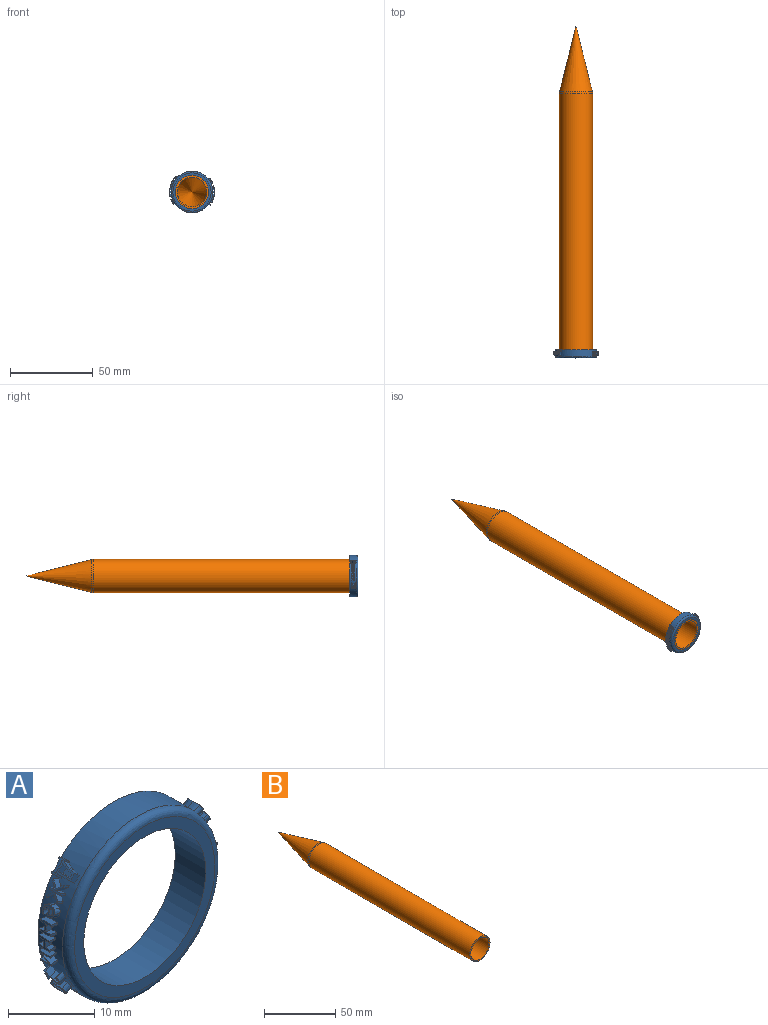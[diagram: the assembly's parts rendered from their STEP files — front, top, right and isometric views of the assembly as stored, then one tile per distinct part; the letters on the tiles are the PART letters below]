
ASSEMBLY  parts=2 mates=1
PART A: 316 faces, bbox 27x5x25 mm
  f0: plane 2.34x0.83mm, normal (0.55,0,0.83), area 2.3mm2, adj f1,f9,f10,f32
  f1: plane 0.98x0.78mm, normal (0,-1,0), area 0.3mm2, adj f0,f2,f10,f32
  f2: plane 2.36x0.83mm, normal (-0.55,0,-0.83), area 2.4mm2, adj f1,f3,f10,f32
  f3: extruded ~0.88x0.62mm, area 0.3mm2, adj f2,f4,f10,f32
  f4: extruded ~0.97x0.76mm, area 0.3mm2, adj f3,f5,f10,f32
  f5: extruded ~0.97x0.76mm, area 0.2mm2, adj f4,f6,f10,f32
  f6: plane 0.84x0.55mm, normal (-0.55,0,-0.83), area 0.2mm2, adj f5,f7,f10,f32
  f7: extruded ~0.97x0.76mm, area 0.2mm2, adj f6,f8,f10,f32
  f8: extruded ~1.09x0.93mm, area 0.5mm2, adj f7,f9,f10,f32
  f9: extruded ~0.92x0.68mm, area 0.5mm2, adj f0,f8,f10,f32
  f10: cylinder r=13.5mm len=2.98mm, axis (0,1,0), area 0.9mm2, adj f0,f1,f2,f3,f4,f5,f6,f7
  f11: extruded ~1.03x0.69mm, area 0.3mm2, adj f12,f24,f30,f32
  f12: extruded ~1.04x0.72mm, area 0.3mm2, adj f11,f13,f30,f32
  f13: extruded ~1.18x1mm, area 0.7mm2, adj f12,f14,f30,f32
  f14: extruded ~1.01x0.66mm, area 0.7mm2, adj f13,f15,f30,f32
  f15: extruded ~1x0.68mm, area 0.7mm2, adj f14,f16,f30,f32
  f16: extruded ~1.16x0.95mm, area 0.6mm2, adj f15,f17,f30,f32
  f17: extruded ~1.14x0.92mm, area 0.6mm2, adj f16,f18,f30,f32
  f18: extruded ~0.99x0.62mm, area 0.6mm2, adj f17,f19,f30,f32
  f19: plane 0.9x0.44mm, normal (0.44,0,0.9), area 0.2mm2, adj f18,f20,f30,f32
  f20: plane 1.54x1.43mm, normal (0,1,0), area 1.2mm2, adj f19,f21,f30,f32
  f21: extruded ~0.97x0.58mm, area 0.5mm2, adj f20,f22,f30,f32
  f22: extruded ~1.09x0.82mm, area 0.5mm2, adj f21,f23,f30,f32
  f23: extruded ~1.16x0.96mm, area 0.6mm2, adj f22,f24,f30,f32
  f24: plane 0.9x0.44mm, normal (0.44,0,0.9), area 0.2mm2, adj f11,f23,f30,f32
  f25: plane 1.31x1.27mm, normal (0,-1,0), area 0.9mm2, adj f26,f29,f30,f31
  f26: extruded ~0.97x0.58mm, area 0.4mm2, adj f25,f27,f30,f31
  f27: extruded ~1.05x0.75mm, area 0.4mm2, adj f26,f28,f30,f31
  f28: extruded ~1.04x0.73mm, area 0.4mm2, adj f27,f29,f30,f31
  f29: extruded ~0.95x0.54mm, area 0.4mm2, adj f25,f28,f30,f31
  f30: cylinder r=13.5mm len=1.83mm, axis (0,1,0), area 1.2mm2, adj f11,f12,f13,f14,f15,f16,f17,f18
  f31: cylinder r=12.5mm len=0.83mm, axis (0,1,0), area 0.4mm2, adj f25,f26,f27,f28,f29
  f32: cylinder r=12.5mm len=25mm, axis (0,1,0), area 286.3mm2, adj f0,f1,f2,f3,f4,f5,f6,f7
  f33: plane 1.21x0.95mm, normal (0.3,0,0.95), area 1.2mm2, adj f32,f34,f51,f60
  f34: plane 1.01x0.5mm, normal (0,1,0), area 0.2mm2, adj f32,f33,f35,f60
  f35: plane 0.97x0.36mm, normal (-0.3,0.21,-0.93), area 0.3mm2, adj f32,f34,f36,f60
  f36: plane 0.96x0.32mm, normal (0,1,0), area 0mm2, adj f32,f35,f37,f60
  f37: extruded ~1.04x0.56mm, area 0.4mm2, adj f32,f36,f38,f60
  f38: extruded ~1.05x0.62mm, area 0.3mm2, adj f32,f37,f39,f60
  f39: extruded ~1.09x0.7mm, area 0.4mm2, adj f32,f38,f40,f60
  f40: extruded ~1.01x0.45mm, area 0.4mm2, adj f32,f39,f41,f60
  f41: extruded ~1.23x1.13mm, area 1.2mm2, adj f32,f40,f42,f60
  f42: plane 1.04x0.59mm, normal (-0.01,-1,-0.03), area 0.3mm2, adj f32,f41,f43,f60
  f43: plane 0.95x0.31mm, normal (-0.3,0,-0.95), area 0.1mm2, adj f32,f42,f44,f60
  f44: extruded ~0.98x0.39mm, area 0.3mm2, adj f32,f43,f45,f60
  f45: extruded ~1.04x0.58mm, area 0.3mm2, adj f32,f44,f46,f60
  f46: extruded ~1.11x0.78mm, area 0.5mm2, adj f32,f45,f47,f60
  f47: plane 0.98x0.38mm, normal (-0.28,0.37,-0.88), area 0.2mm2, adj f32,f46,f48,f60
  f48: extruded ~1.05x0.58mm, area 0.3mm2, adj f32,f47,f49,f60
  f49: extruded ~1.05x0.6mm, area 0.3mm2, adj f32,f48,f50,f60
  f50: extruded ~1.11x0.75mm, area 0.5mm2, adj f32,f49,f51,f60
  f51: extruded ~1.01x0.45mm, area 0.5mm2, adj f32,f33,f50,f60
  f52: extruded ~1x0.44mm, area 0.3mm2, adj f53,f59,f60,f61
  f53: extruded ~1.1x0.74mm, area 0.5mm2, adj f52,f54,f60,f61
  f54: plane 1.03x0.56mm, normal (0.01,1,0.04), area 0.3mm2, adj f53,f55,f60,f61
  f55: plane 0.95x0.31mm, normal (-0.3,0,-0.95), area 0.2mm2, adj f54,f56,f60,f61
  f56: extruded ~1x0.44mm, area 0.4mm2, adj f55,f57,f60,f61
  f57: extruded ~1.07x0.68mm, area 0.4mm2, adj f56,f58,f60,f61
  f58: extruded ~1.03x0.54mm, area 0.3mm2, adj f57,f59,f60,f61
  f59: extruded ~0.98x0.39mm, area 0.2mm2, adj f52,f58,f60,f61
  f60: cylinder r=13.5mm len=1.83mm, axis (0,1,0), area 1.2mm2, adj f33,f34,f35,f36,f37,f38,f39,f40
  f61: cylinder r=12.5mm len=0.83mm, axis (0,1,0), area 0.4mm2, adj f52,f53,f54,f55,f56,f57,f58,f59
  f62: extruded ~1.02x0.49mm, area 0.5mm2, adj f32,f63,f78,f79
  f63: extruded ~1.08x0.64mm, area 0.5mm2, adj f32,f62,f64,f79
  f64: extruded ~1.04x0.49mm, area 0.3mm2, adj f32,f63,f65,f79
  f65: extruded ~1.03x0.39mm, area 0.3mm2, adj f32,f64,f66,f79
  f66: plane 0.99x0.17mm, normal (0,-1,0), area 0mm2, adj f32,f65,f67,f79
  f67: plane 1x0.24mm, normal (0.16,-0.18,0.97), area 0.2mm2, adj f32,f66,f68,f79
  f68: plane 1.03x0.37mm, normal (0,-1,0), area 0.2mm2, adj f32,f67,f69,f79
  f69: plane 1.77x0.99mm, normal (-0.16,0,-0.99), area 1.8mm2, adj f32,f68,f70,f79
  f70: plane 1.04x0.42mm, normal (0,1,0), area 0.3mm2, adj f32,f69,f71,f79
  f71: plane 0.99x0.93mm, normal (0.16,0,0.99), area 0.9mm2, adj f32,f70,f72,f79
  f72: extruded ~1.01x0.5mm, area 0.5mm2, adj f32,f71,f73,f79
  f73: extruded ~1.06x0.56mm, area 0.4mm2, adj f32,f72,f74,f79
  f74: extruded ~1.04x0.46mm, area 0.3mm2, adj f32,f73,f75,f79
  f75: extruded ~1.01x0.32mm, area 0.3mm2, adj f32,f74,f76,f79
  f76: plane 1.14x0.99mm, normal (-0.16,0,-0.99), area 1.1mm2, adj f32,f75,f77,f79
  f77: plane 1.02x0.43mm, normal (0,1,0), area 0.3mm2, adj f32,f76,f78,f79
  f78: plane 1.15x0.99mm, normal (0.16,0,0.99), area 1.2mm2, adj f32,f62,f77,f79
  f79: cylinder r=13.5mm len=1.8mm, axis (0,1,0), area 1.1mm2, adj f62,f63,f64,f65,f66,f67,f68,f69
  f80: extruded ~1.01x0.49mm, area 0.5mm2, adj f32,f81,f96,f97
  f81: extruded ~1.02x0.48mm, area 0.5mm2, adj f32,f80,f82,f97
  f82: extruded ~1x0.33mm, area 0.3mm2, adj f32,f81,f83,f97
  f83: extruded ~1.01x0.23mm, area 0.3mm2, adj f32,f82,f84,f97
  f84: plane 1x0.01mm, normal (0,-1,0), area 0mm2, adj f32,f83,f85,f97
  f85: plane 1x0.24mm, normal (0,-0.18,0.98), area 0.2mm2, adj f32,f84,f86,f97
  f86: plane 1.01x0.22mm, normal (0,-1,0), area 0.2mm2, adj f32,f85,f87,f97
  f87: plane 1.77x1mm, normal (0,0,-1), area 1.8mm2, adj f32,f86,f88,f97
  f88: plane 1.01x0.27mm, normal (0,1,0), area 0.3mm2, adj f32,f87,f89,f97
  f89: plane 1x0.93mm, normal (0,0,1), area 0.9mm2, adj f32,f88,f90,f97
  f90: extruded ~1x0.5mm, area 0.5mm2, adj f32,f89,f91,f97
  f91: extruded ~1x0.41mm, area 0.4mm2, adj f32,f90,f92,f97
  f92: extruded ~1.01x0.31mm, area 0.3mm2, adj f32,f91,f93,f97
  f93: extruded ~1x0.32mm, area 0.3mm2, adj f32,f92,f94,f97
  f94: plane 1.14x1mm, normal (0,0,-1), area 1.1mm2, adj f32,f93,f95,f97
  f95: plane 1.01x0.27mm, normal (0,1,0), area 0.3mm2, adj f32,f94,f96,f97
  f96: plane 1.15x1mm, normal (0,0,1), area 1.2mm2, adj f32,f80,f95,f97
  f97: cylinder r=13.5mm len=1.8mm, axis (0,1,0), area 1.1mm2, adj f80,f81,f82,f83,f84,f85,f86,f87
  f98: plane 1.77x0.99mm, normal (0.11,0,-0.99), area 1.8mm2, adj f32,f99,f101,f102
  f99: plane 1.02x0.38mm, normal (0,1,0), area 0.3mm2, adj f32,f98,f100,f102
  f100: plane 1.77x0.99mm, normal (-0.11,0,0.99), area 1.8mm2, adj f32,f99,f101,f102
  f101: plane 1.02x0.38mm, normal (0,-1,0), area 0.3mm2, adj f32,f98,f100,f102
  f102: cylinder r=13.5mm len=1.77mm, axis (0,1,0), area 0.5mm2, adj f98,f99,f100,f101
  f103: extruded ~1.01x0.22mm, area 0.1mm2, adj f32,f104,f110,f111
  f104: extruded ~1x0.16mm, area 0.1mm2, adj f32,f103,f105,f111
  f105: extruded ~1x0.16mm, area 0.1mm2, adj f32,f104,f106,f111
  f106: extruded ~1.01x0.22mm, area 0.1mm2, adj f32,f105,f107,f111
  f107: extruded ~1.01x0.22mm, area 0.1mm2, adj f32,f106,f108,f111
  f108: extruded ~1x0.15mm, area 0.1mm2, adj f32,f107,f109,f111
  f109: extruded ~1x0.15mm, area 0.1mm2, adj f32,f108,f110,f111
  f110: extruded ~1.01x0.22mm, area 0.1mm2, adj f32,f103,f109,f111
  f111: cylinder r=13.5mm len=0.36mm, axis (0,1,0), area 0.1mm2, adj f103,f104,f105,f106,f107,f108,f109,f110
  f112: extruded ~1.05x0.48mm, area 0.3mm2, adj f32,f113,f125,f131
  f113: extruded ~1.05x0.52mm, area 0.3mm2, adj f32,f112,f114,f131
  f114: extruded ~1.12x0.82mm, area 0.7mm2, adj f32,f113,f115,f131
  f115: extruded ~1.04x0.66mm, area 0.7mm2, adj f32,f114,f116,f131
  f116: extruded ~1.03x0.68mm, area 0.7mm2, adj f32,f115,f117,f131
  f117: extruded ~1.11x0.77mm, area 0.6mm2, adj f32,f116,f118,f131
  f118: extruded ~1.1x0.73mm, area 0.6mm2, adj f32,f117,f119,f131
  f119: extruded ~1.03x0.58mm, area 0.6mm2, adj f32,f118,f120,f131
  f120: plane 0.98x0.22mm, normal (-0.22,0,0.98), area 0.2mm2, adj f32,f119,f121,f131
  f121: plane 1.4x1.25mm, normal (0,1,0), area 1.2mm2, adj f32,f120,f122,f131
  f122: extruded ~1.02x0.47mm, area 0.5mm2, adj f32,f121,f123,f131
  f123: extruded ~1.07x0.63mm, area 0.5mm2, adj f32,f122,f124,f131
  f124: extruded ~1.11x0.77mm, area 0.6mm2, adj f32,f123,f125,f131
  f125: plane 0.98x0.24mm, normal (-0.22,0,0.98), area 0.2mm2, adj f32,f112,f124,f131
  f126: plane 1.18x1.12mm, normal (0,-1,0), area 0.9mm2, adj f127,f130,f131,f132
  f127: extruded ~1.01x0.38mm, area 0.4mm2, adj f126,f128,f131,f132
  f128: extruded ~1.05x0.55mm, area 0.4mm2, adj f127,f129,f131,f132
  f129: extruded ~1.05x0.53mm, area 0.4mm2, adj f128,f130,f131,f132
  f130: extruded ~1x0.39mm, area 0.4mm2, adj f126,f129,f131,f132
  f131: cylinder r=13.5mm len=1.83mm, axis (0,1,0), area 1.2mm2, adj f112,f113,f114,f115,f116,f117,f118,f119
  f132: cylinder r=12.5mm len=0.9mm, axis (0,1,0), area 0.4mm2, adj f126,f127,f128,f129,f130
  f133: plane 0.9x0.45mm, normal (-0.45,0,0.9), area 0mm2, adj f32,f134,f152,f153
  f134: plane 1.12x0.91mm, normal (-0.31,0.71,0.63), area 0.7mm2, adj f32,f133,f135,f153
  f135: extruded ~1.12x0.87mm, area 0.7mm2, adj f32,f134,f136,f153
  f136: extruded ~0.96x0.56mm, area 0.5mm2, adj f32,f135,f137,f153
  f137: extruded ~0.99x0.62mm, area 0.5mm2, adj f32,f136,f138,f153
  f138: extruded ~1.14x0.92mm, area 0.6mm2, adj f32,f137,f139,f153
  f139: extruded ~1.23x1.09mm, area 0.8mm2, adj f32,f138,f140,f153
  f140: plane 0.95x0.58mm, normal (0.35,0.61,-0.71), area 0.2mm2, adj f32,f139,f141,f153
  f141: extruded ~1.04x0.71mm, area 0.3mm2, adj f32,f140,f142,f153
  f142: extruded ~1.02x0.7mm, area 0.3mm2, adj f32,f141,f143,f153
  f143: extruded ~1.04x0.73mm, area 0.3mm2, adj f32,f142,f144,f153
  f144: extruded ~0.95x0.55mm, area 0.3mm2, adj f32,f143,f145,f153
  f145: extruded ~0.92x0.49mm, area 0.3mm2, adj f32,f144,f146,f153
  f146: extruded ~0.96x0.57mm, area 0.3mm2, adj f32,f145,f147,f153
  f147: extruded ~1.06x0.78mm, area 0.6mm2, adj f32,f146,f148,f153
  f148: plane 1.15x1.01mm, normal (0.32,-0.71,-0.63), area 0.9mm2, adj f32,f147,f149,f153
  f149: plane 0.9x0.45mm, normal (0.45,0,-0.9), area 0.2mm2, adj f32,f148,f150,f153
  f150: plane 1.84x1.58mm, normal (0,1,0), area 1.6mm2, adj f32,f149,f151,f153
  f151: plane 0.9x0.45mm, normal (-0.45,0,0.9), area 0.2mm2, adj f32,f150,f152,f153
  f152: plane 1.53x1.45mm, normal (0,-1,0), area 1.2mm2, adj f32,f133,f151,f153
  f153: cylinder r=13.5mm len=2.39mm, axis (0,1,0), area 1.2mm2, adj f133,f134,f135,f136,f137,f138,f139,f140
  f154: extruded ~1.16x1.06mm, area 0.7mm2, adj f32,f155,f161,f170
  f155: extruded ~0.94x0.9mm, area 0.9mm2, adj f32,f154,f156,f170
  f156: extruded ~0.94x0.91mm, area 0.9mm2, adj f32,f155,f157,f170
  f157: extruded ~1.17x1.07mm, area 0.7mm2, adj f32,f156,f158,f170
  f158: extruded ~1.16x1.06mm, area 0.7mm2, adj f32,f157,f159,f170
  f159: extruded ~0.94x0.91mm, area 0.9mm2, adj f32,f158,f160,f170
  f160: extruded ~0.94x0.91mm, area 0.9mm2, adj f32,f159,f161,f170
  f161: extruded ~1.17x1.06mm, area 0.7mm2, adj f32,f154,f160,f170
  f162: extruded ~1.04x0.9mm, area 0.5mm2, adj f163,f169,f170,f171
  f163: extruded ~0.89x0.74mm, area 0.8mm2, adj f162,f164,f170,f171
  f164: extruded ~0.89x0.75mm, area 0.8mm2, adj f163,f165,f170,f171
  f165: extruded ~1.04x0.9mm, area 0.5mm2, adj f164,f166,f170,f171
  f166: extruded ~1.04x0.9mm, area 0.5mm2, adj f165,f167,f170,f171
  f167: extruded ~0.89x0.75mm, area 0.8mm2, adj f166,f168,f170,f171
  f168: extruded ~0.89x0.75mm, area 0.8mm2, adj f167,f169,f170,f171
  f169: extruded ~1.04x0.9mm, area 0.5mm2, adj f162,f168,f170,f171
  f170: cylinder r=13.5mm len=2.43mm, axis (0,1,0), area 1.3mm2, adj f154,f155,f156,f157,f158,f159,f160,f161
  f171: cylinder r=12.5mm len=1.97mm, axis (0,1,0), area 1.5mm2, adj f162,f163,f164,f165,f166,f167,f168,f169
  f172: plane 0.94x0.89mm, normal (0,-1,0), area 0.3mm2, adj f32,f173,f184,f190
  f173: plane 0.86x0.76mm, normal (-0.65,0,-0.76), area 0.9mm2, adj f32,f172,f174,f190
  f174: plane 0.92x0.86mm, normal (0,1,0), area 0.3mm2, adj f32,f173,f175,f190
  f175: plane 0.76x0.65mm, normal (0.65,0,0.76), area 0.6mm2, adj f32,f174,f176,f190
  f176: plane 1.89x1.84mm, normal (0,1,0), area 1.6mm2, adj f32,f175,f177,f190
  f177: plane 0.76x0.65mm, normal (-0.65,0,-0.76), area 0.6mm2, adj f32,f176,f178,f190
  f178: plane 0.95x0.84mm, normal (0,1,0), area 0.3mm2, adj f32,f177,f179,f190
  f179: plane 0.86x0.76mm, normal (0.65,0,0.76), area 0.9mm2, adj f32,f178,f180,f190
  f180: plane 0.89x0.78mm, normal (0,-1,0), area 0.2mm2, adj f32,f179,f181,f190
  f181: extruded ~1.06x1.02mm, area 1.1mm2, adj f32,f180,f182,f190
  f182: extruded ~1.09x0.89mm, area 1.1mm2, adj f32,f181,f183,f190
  f183: plane 1.46x1.44mm, normal (0,-1,0), area 1.1mm2, adj f32,f182,f184,f190
  f184: plane 2.11x0.76mm, normal (-0.65,0,-0.76), area 2.1mm2, adj f32,f172,f183,f190
  f185: extruded ~0.94x0.89mm, area 1mm2, adj f186,f189,f190,f191
  f186: plane 1.11x1.06mm, normal (0,1,0), area 0.5mm2, adj f185,f187,f190,f191
  f187: plane 1.86x0.76mm, normal (0.65,0,0.76), area 1.9mm2, adj f186,f188,f190,f191
  f188: plane 1.5x1.49mm, normal (0,-1,0), area 1.1mm2, adj f187,f189,f190,f191
  f189: extruded ~1.02x0.96mm, area 1mm2, adj f185,f188,f190,f191
  f190: cylinder r=13.5mm len=2.97mm, axis (0,1,0), area 2.2mm2, adj f172,f173,f174,f175,f176,f177,f178,f179
  f191: cylinder r=12.5mm len=1.86mm, axis (0,1,0), area 1.5mm2, adj f185,f186,f187,f188,f189
  f192: plane 1.26x1.11mm, normal (-0.37,-0.65,-0.67), area 1.1mm2, adj f32,f193,f209,f210
  f193: plane 0.88x0.86mm, normal (0.48,0,0.87), area 0.9mm2, adj f32,f192,f194,f210
  f194: plane 1x0.7mm, normal (0,-1,0), area 0.2mm2, adj f32,f193,f195,f210
  f195: plane 0.87x0.86mm, normal (-0.48,0,-0.87), area 0.9mm2, adj f32,f194,f196,f210
  f196: plane 1.21x1.14mm, normal (0.37,-0.65,0.67), area 1.1mm2, adj f32,f195,f197,f210
  f197: plane 1x0.75mm, normal (0,-1,0), area 0.3mm2, adj f32,f196,f198,f210
  f198: plane 1.2x1.15mm, normal (-0.37,0.65,-0.66), area 1.1mm2, adj f32,f197,f199,f210
  f199: plane 1.23x1.21mm, normal (-0.36,-0.66,-0.66), area 1.2mm2, adj f32,f198,f200,f210
  f200: plane 1.01x0.77mm, normal (0,1,0), area 0.3mm2, adj f32,f199,f201,f210
  f201: plane 1.23x1.18mm, normal (0.37,0.66,0.66), area 1.2mm2, adj f32,f200,f202,f210
  f202: plane 0.9x0.87mm, normal (-0.48,0,-0.87), area 0.9mm2, adj f32,f201,f203,f210
  f203: plane 1x0.7mm, normal (0,1,0), area 0.2mm2, adj f32,f202,f204,f210
  f204: plane 0.9x0.88mm, normal (0.48,0,0.87), area 0.9mm2, adj f32,f203,f205,f210
  f205: plane 1.29x1.15mm, normal (-0.37,0.66,-0.66), area 1.2mm2, adj f32,f204,f206,f210
  f206: plane 1.05x0.74mm, normal (0,1,0), area 0.3mm2, adj f32,f205,f207,f210
  f207: plane 1.32x1.16mm, normal (0.36,-0.66,0.66), area 1.2mm2, adj f32,f206,f208,f210
  f208: plane 1.28x1.11mm, normal (0.37,0.65,0.66), area 1.1mm2, adj f32,f207,f209,f210
  f209: plane 1.04x0.73mm, normal (0,-1,0), area 0.3mm2, adj f32,f192,f208,f210
  f210: cylinder r=13.5mm len=2.11mm, axis (0,1,0), area 1.5mm2, adj f192,f193,f194,f195,f196,f197,f198,f199
  f211: extruded ~1.04x0.58mm, area 0.3mm2, adj f32,f212,f224,f230
  f212: extruded ~1.05x0.61mm, area 0.3mm2, adj f32,f211,f213,f230
  f213: extruded ~1.16x0.91mm, area 0.7mm2, adj f32,f212,f214,f230
  f214: extruded ~1.03x0.66mm, area 0.7mm2, adj f32,f213,f215,f230
  f215: extruded ~1.03x0.68mm, area 0.7mm2, adj f32,f214,f216,f230
  f216: extruded ~1.14x0.86mm, area 0.6mm2, adj f32,f215,f217,f230
  f217: extruded ~1.13x0.82mm, area 0.6mm2, adj f32,f216,f218,f230
  f218: extruded ~1.02x0.58mm, area 0.6mm2, adj f32,f217,f219,f230
  f219: plane 0.95x0.32mm, normal (-0.32,0,-0.95), area 0.2mm2, adj f32,f218,f220,f230
  f220: plane 1.48x1.33mm, normal (0,1,0), area 1.2mm2, adj f32,f219,f221,f230
  f221: extruded ~1x0.47mm, area 0.5mm2, adj f32,f220,f222,f230
  f222: extruded ~1.09x0.72mm, area 0.5mm2, adj f32,f221,f223,f230
  f223: extruded ~1.14x0.86mm, area 0.6mm2, adj f32,f222,f224,f230
  f224: plane 0.95x0.32mm, normal (-0.32,0,-0.95), area 0.2mm2, adj f32,f211,f223,f230
  f225: plane 1.24x1.2mm, normal (0,-1,0), area 0.9mm2, adj f226,f229,f230,f231
  f226: extruded ~1x0.46mm, area 0.4mm2, adj f225,f227,f230,f231
  f227: extruded ~1.06x0.64mm, area 0.4mm2, adj f226,f228,f230,f231
  f228: extruded ~1.06x0.63mm, area 0.4mm2, adj f227,f229,f230,f231
  f229: extruded ~0.99x0.43mm, area 0.4mm2, adj f225,f228,f230,f231
  f230: cylinder r=13.5mm len=1.83mm, axis (0,1,0), area 1.2mm2, adj f211,f212,f213,f214,f215,f216,f217,f218
  f231: cylinder r=12.5mm len=0.88mm, axis (0,1,0), area 0.4mm2, adj f225,f226,f227,f228,f229
  f232: plane 1.04x0.43mm, normal (0,1,0), area 0.3mm2, adj f32,f233,f243,f244
  f233: plane 0.99x0.8mm, normal (-0.17,0,-0.99), area 0.8mm2, adj f32,f232,f234,f244
  f234: plane 1.15x1.14mm, normal (0,1,0), area 1mm2, adj f32,f233,f235,f244
  f235: plane 0.99x0.8mm, normal (0.17,0,0.99), area 0.8mm2, adj f32,f234,f236,f244
  f236: plane 1.02x0.43mm, normal (0,1,0), area 0.3mm2, adj f32,f235,f237,f244
  f237: plane 1.77x0.99mm, normal (-0.17,0,-0.99), area 1.8mm2, adj f32,f236,f238,f244
  f238: plane 1.02x0.43mm, normal (0,-1,0), area 0.3mm2, adj f32,f237,f239,f244
  f239: plane 0.99x0.74mm, normal (0.17,0,0.99), area 0.7mm2, adj f32,f238,f240,f244
  f240: plane 1.15x1.14mm, normal (0,-1,0), area 1mm2, adj f32,f239,f241,f244
  f241: plane 0.99x0.74mm, normal (-0.17,0,-0.99), area 0.7mm2, adj f32,f240,f242,f244
  f242: plane 1.04x0.43mm, normal (0,-1,0), area 0.3mm2, adj f32,f241,f243,f244
  f243: plane 1.77x0.99mm, normal (0.17,0,0.99), area 1.8mm2, adj f32,f232,f242,f244
  f244: cylinder r=13.5mm len=1.77mm, axis (0,1,0), area 1.2mm2, adj f232,f233,f234,f235,f236,f237,f238,f239
  f245: plane 1.02x0.27mm, normal (0,1,0), area 0.3mm2, adj f32,f246,f256,f257
  f246: plane 1x0.8mm, normal (-0.01,0,-1), area 0.8mm2, adj f32,f245,f247,f257
  f247: plane 1.01x1mm, normal (0,1,0), area 1mm2, adj f32,f246,f248,f257
  f248: plane 1x0.8mm, normal (0.01,0,1), area 0.8mm2, adj f32,f247,f249,f257
  f249: plane 1.01x0.27mm, normal (0,1,0), area 0.3mm2, adj f32,f248,f250,f257
  f250: plane 1.77x1mm, normal (-0.01,0,-1), area 1.8mm2, adj f32,f249,f251,f257
  f251: plane 1.01x0.27mm, normal (0,-1,0), area 0.3mm2, adj f32,f250,f252,f257
  f252: plane 1x0.74mm, normal (0.01,0,1), area 0.7mm2, adj f32,f251,f253,f257
  f253: plane 1.01x1mm, normal (0,-1,0), area 1mm2, adj f32,f252,f254,f257
  f254: plane 1x0.74mm, normal (-0.01,0,-1), area 0.7mm2, adj f32,f253,f255,f257
  f255: plane 1.02x0.27mm, normal (0,-1,0), area 0.3mm2, adj f32,f254,f256,f257
  f256: plane 1.77x1mm, normal (0.01,0,1), area 1.8mm2, adj f32,f245,f255,f257
  f257: cylinder r=13.5mm len=1.77mm, axis (0,1,0), area 1.2mm2, adj f245,f246,f247,f248,f249,f250,f251,f252
  f258: plane 1.03x0.49mm, normal (0,1,0), area 0.3mm2, adj f32,f259,f271,f272
  f259: plane 1.5x1.14mm, normal (0.13,0.54,-0.83), area 1.8mm2, adj f32,f258,f260,f272
  f260: plane 0.99x0.21mm, normal (-0.16,-0.04,0.99), area 0.2mm2, adj f32,f259,f261,f272
  f261: plane 0.99x0.21mm, normal (-0.16,-0.02,0.99), area 0.2mm2, adj f32,f260,f262,f272
  f262: plane 1.08x0.99mm, normal (-0.16,0,0.99), area 1.1mm2, adj f32,f261,f263,f272
  f263: plane 1.04x0.4mm, normal (0,1,0), area 0.3mm2, adj f32,f262,f264,f272
  f264: plane 1.77x0.99mm, normal (0.16,0,-0.99), area 1.8mm2, adj f32,f263,f265,f272
  f265: plane 1.06x0.48mm, normal (0,-1,0), area 0.3mm2, adj f32,f264,f266,f272
  f266: plane 1.51x1.14mm, normal (-0.13,-0.54,0.83), area 1.8mm2, adj f32,f265,f267,f272
  f267: plane 0.99x0.16mm, normal (0.16,0.06,-0.99), area 0.1mm2, adj f32,f266,f268,f272
  f268: plane 0.99x0.29mm, normal (0.16,0.04,-0.99), area 0.3mm2, adj f32,f267,f269,f272
  f269: plane 1.12x0.99mm, normal (0.16,0,-0.99), area 1.1mm2, adj f32,f268,f270,f272
  f270: plane 1.02x0.41mm, normal (0,-1,0), area 0.3mm2, adj f32,f269,f271,f272
  f271: plane 1.77x0.99mm, normal (-0.16,0,0.99), area 1.8mm2, adj f32,f258,f270,f272
  f272: cylinder r=13.5mm len=1.77mm, axis (0,1,0), area 1.3mm2, adj f258,f259,f260,f261,f262,f263,f264,f265
  f273: plane 0.92x0.39mm, normal (0.39,0,-0.92), area 0mm2, adj f32,f274,f292,f293
  f274: plane 1.12x0.87mm, normal (0.28,0.71,-0.64), area 0.7mm2, adj f32,f273,f275,f293
  f275: extruded ~1.11x0.83mm, area 0.7mm2, adj f32,f274,f276,f293
  f276: extruded ~0.98x0.51mm, area 0.5mm2, adj f32,f275,f277,f293
  f277: extruded ~1x0.57mm, area 0.5mm2, adj f32,f276,f278,f293
  f278: extruded ~1.13x0.88mm, area 0.6mm2, adj f32,f277,f279,f293
  f279: extruded ~1.22x1.06mm, area 0.8mm2, adj f32,f278,f280,f293
  f280: plane 0.97x0.53mm, normal (-0.31,0.61,0.72), area 0.2mm2, adj f32,f279,f281,f293
  f281: extruded ~1.05x0.67mm, area 0.3mm2, adj f32,f280,f282,f293
  f282: extruded ~1.03x0.65mm, area 0.3mm2, adj f32,f281,f283,f293
  f283: extruded ~1.05x0.69mm, area 0.3mm2, adj f32,f282,f284,f293
  f284: extruded ~0.97x0.5mm, area 0.3mm2, adj f32,f283,f285,f293
  f285: extruded ~0.94x0.44mm, area 0.3mm2, adj f32,f284,f286,f293
  f286: extruded ~0.98x0.52mm, area 0.3mm2, adj f32,f285,f287,f293
  f287: extruded ~1.07x0.74mm, area 0.6mm2, adj f32,f286,f288,f293
  f288: plane 1.14x0.98mm, normal (-0.28,-0.71,0.65), area 0.9mm2, adj f32,f287,f289,f293
  f289: plane 0.92x0.4mm, normal (-0.39,0,0.92), area 0.2mm2, adj f32,f288,f290,f293
  f290: plane 1.82x1.53mm, normal (0,1,0), area 1.6mm2, adj f32,f289,f291,f293
  f291: plane 0.92x0.4mm, normal (0.39,0,-0.92), area 0.2mm2, adj f32,f290,f292,f293
  f292: plane 1.5x1.41mm, normal (0,-1,0), area 1.2mm2, adj f32,f273,f291,f293
  f293: cylinder r=13.5mm len=2.39mm, axis (0,1,0), area 1.2mm2, adj f273,f274,f275,f276,f277,f278,f279,f280
  f294: extruded ~1.17x1.03mm, area 0.7mm2, adj f32,f295,f301,f310
  f295: extruded ~0.96x0.9mm, area 0.9mm2, adj f32,f294,f296,f310
  f296: extruded ~0.96x0.91mm, area 0.9mm2, adj f32,f295,f297,f310
  f297: extruded ~1.17x1.04mm, area 0.7mm2, adj f32,f296,f298,f310
  f298: extruded ~1.17x1.03mm, area 0.7mm2, adj f32,f297,f299,f310
  f299: extruded ~0.96x0.91mm, area 0.9mm2, adj f32,f298,f300,f310
  f300: extruded ~0.96x0.91mm, area 0.9mm2, adj f32,f299,f301,f310
  f301: extruded ~1.17x1.04mm, area 0.7mm2, adj f32,f294,f300,f310
  f302: extruded ~1.06x0.86mm, area 0.5mm2, adj f303,f309,f310,f311
  f303: extruded ~0.92x0.74mm, area 0.8mm2, adj f302,f304,f310,f311
  f304: extruded ~0.92x0.75mm, area 0.8mm2, adj f303,f305,f310,f311
  f305: extruded ~1.06x0.86mm, area 0.5mm2, adj f304,f306,f310,f311
  f306: extruded ~1.06x0.86mm, area 0.5mm2, adj f305,f307,f310,f311
  f307: extruded ~0.92x0.75mm, area 0.8mm2, adj f306,f308,f310,f311
  f308: extruded ~0.92x0.75mm, area 0.8mm2, adj f307,f309,f310,f311
  f309: extruded ~1.06x0.86mm, area 0.5mm2, adj f302,f308,f310,f311
  f310: cylinder r=13.5mm len=2.43mm, axis (0,1,0), area 1.3mm2, adj f294,f295,f296,f297,f298,f299,f300,f301
  f311: cylinder r=12.5mm len=1.97mm, axis (0,1,0), area 1.5mm2, adj f302,f303,f304,f305,f306,f307,f308,f309
  f312: plane 23.01x23.01mm, normal (0,-1,0), area 101.3mm2, adj f314,f315
  f313: plane 25x25mm, normal (0,1,0), area 176.7mm2, adj f32,f314
  f314: cylinder r=10mm len=20mm, axis (0,1,0), area 314.2mm2, adj f312,f313
  f315: bspline ~24.99x24.97mm, area 124.2mm2, adj f32,f312
PART B: 8 faces, bbox 21.6x200x21.6 mm
  f0: cylinder r=9mm len=160mm, axis (0,1,0), area 9047.8mm2, adj f2,f4
  f1: cylinder r=10mm len=159.38mm, axis (0,1,0), area 10014.4mm2, adj f2,f5
  f2: plane 20x20mm, normal (0,-1,0), area 59.7mm2, adj f0,f1
  f3: cone r=10mm half-angle=14deg, axis (0,-1,0), area 1256.9mm2, adj f5
  f4: plane 18x18mm, normal (0,-1,0), area 2.7mm2, adj f0,f6
  f5: torus R=5mm, axis (0,-1,0), area 76.6mm2, adj f1,f3
  f6: torus R=5mm, axis (0,-1,0), area 20.3mm2, adj f4,f7
  f7: cone r=9.03mm half-angle=14deg, axis (0,-1,0), area 1021.5mm2, adj f6
PLACE A t=(-14.96,54.55,90.97)mm
PLACE B t=(-14.96,209.55,90.97)mm
MATE fastened B.f0 <-> A.f314  axis (0,-1,0) through (-14.96,49.55,90.97)mm
